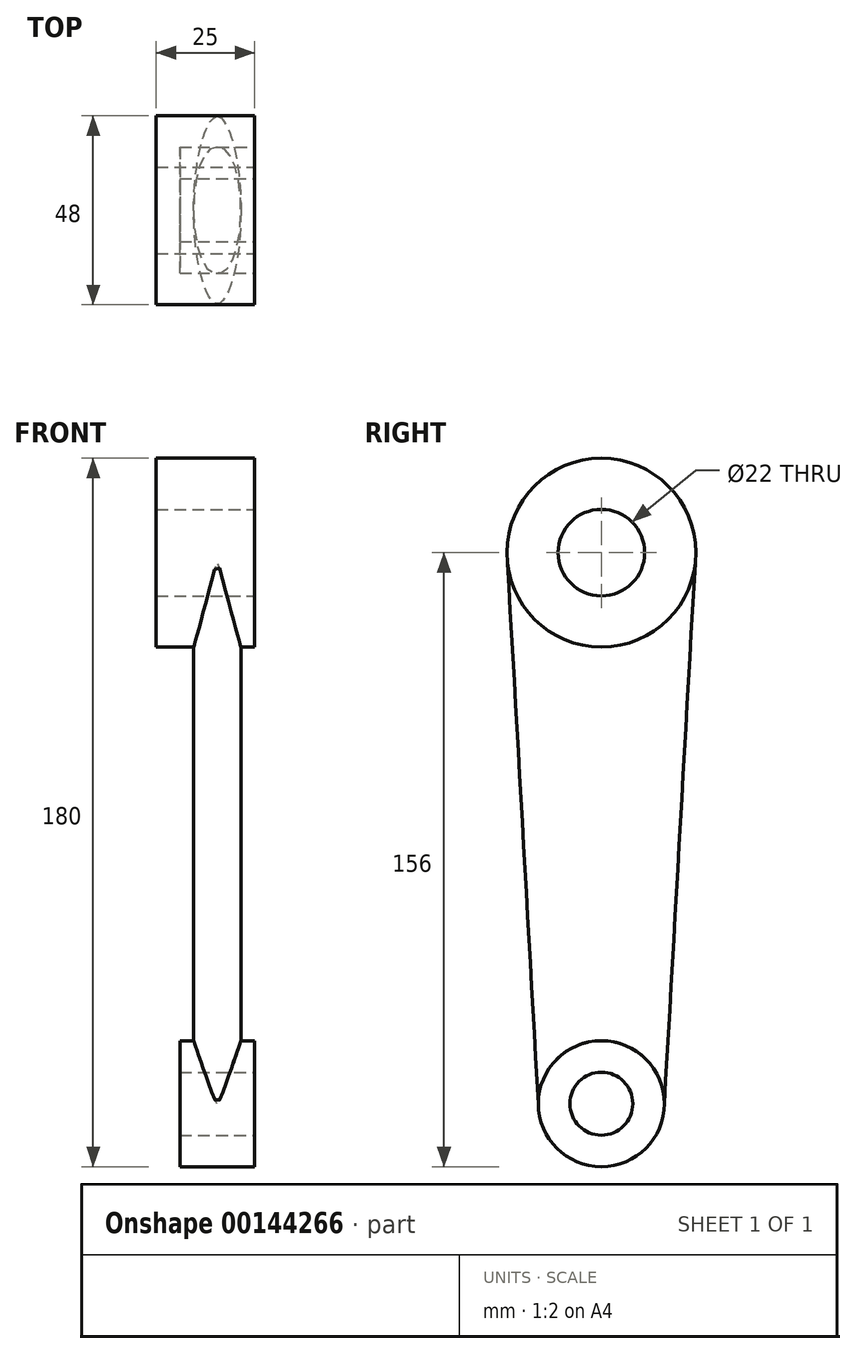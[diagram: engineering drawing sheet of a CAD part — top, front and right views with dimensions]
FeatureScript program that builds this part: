
annotation { "Feature Type Name" : "Feature", "Feature Type Description" : "" }
export const myFeature = defineFeature(function(context is Context, id is Id, definition is map)
    precondition{}
    {
        {
            var Q0;
            Q0=qCreatedBy(makeId("Right.planeOp"),FACE);
            var sketch = newSketch(context, id + "F0", { "sketchPlane" : qUnion([Q0])});
            skCircle(sketch, "E0", {"center": v(0, 0) * mm, "radius": 16 * mm});
            skCircle(sketch, "E1", {"center": v(0, 140) * mm, "radius": 24 * mm});
            skSolve(sketch);
        }
        {
            var Q0;
            Q0=makeQuery(id+"F0.imprint","IMPRINT",FACE,{"disambiguationData":[TD([[makeQuery(id+"F0.imprint","IMPRINT",EDGE,{"derivedFrom":sQuery(id+"F0.wireOp",EDGE,"E1")}),1.0]])]});
            extrude(context, id + "F1", {"entities" : qUnion([Q0]), "oppositeDirection" : true, "depth" : 25 * mm});
        }
        {
            var Q0;
            Q0=makeQuery(id+"F0.imprint","IMPRINT",FACE,{"disambiguationData":[TD([[makeQuery(id+"F0.imprint","IMPRINT",EDGE,{"derivedFrom":sQuery(id+"F0.wireOp",EDGE,"E0")}),1.0]])]});
            extrude(context, id + "F2", {"entities" : qUnion([Q0]), "oppositeDirection" : true, "depth" : 19 * mm});
        }
        {
            var Q0;
            Q0=qCreatedBy(makeId("Top.planeOp"),FACE);
            var sketch = newSketch(context, id + "F3", { "sketchPlane" : qUnion([Q0])});
            skEllipse(sketch, "E2", {"center": v(-9.5, 0) * mm, "majorRadius": 16 * mm, "minorRadius": 6 * mm, "majorAxis": v(0, 1)});
            skPoint(sketch, "E3", {"position": v(-15.5, 0) * mm});
            skLineSegment(sketch, "E4", {"start": v(-19, 16) * mm, "end": v(0, 16) * mm, "construction": true});
            skSolve(sketch);
        }
        {
            var Q0;
            Q0=sQuery(id+"F0.wireOp",VERTEX,"E1.center");
            var Q1;
            Q1=qCreatedBy(makeId("Top.planeOp"),FACE);
            cPlane(context, id + "F4", {"entities" : qUnion([Q0, Q1]), "cplaneType" : CPlaneType.PLANE_POINT, "offset" : 25 * mm, "width" : 150 * mm, "height" : 150 * mm});
        }
        {
            var Q0;
            Q0=qCreatedBy(id+"F4.planeOp",FACE);
            var sketch = newSketch(context, id + "F5", { "sketchPlane" : qUnion([Q0])});
            skEllipse(sketch, "E5", {"center": v(-9.5, 0) * mm, "majorRadius": 24 * mm, "minorRadius": 6 * mm, "majorAxis": v(0, 1)});
            skLineSegment(sketch, "E6", {"start": v(-25, 24) * mm, "end": v(0, 24) * mm, "construction": true});
            skSolve(sketch);
        }
        {
            var Q2;
            Q2=makeQuery(id+"F5.imprint","IMPRINT",FACE,{"disambiguationData":[TD([[makeQuery(id+"F5.imprint","IMPRINT",EDGE,{"derivedFrom":sQuery(id+"F5.wireOp",EDGE,"E5")}),1.0]])]});
            var Q3;
            Q3=makeQuery(id+"F3.imprint","IMPRINT",FACE,{"disambiguationData":[TD([[makeQuery(id+"F3.imprint","IMPRINT",EDGE,{"derivedFrom":sQuery(id+"F3.wireOp",EDGE,"E2")}),1.0]])]});
            loft(context, id + "F6", {"operationType" : NewBodyOperationType.ADD, "sheetProfilesArray" : [{ "sheetProfileEntities" : qUnion([Q2]) }, { "sheetProfileEntities" : qUnion([Q3]) }]});
        }
        {
            var Q0;
            Q0=makeQuery(id+"F0.imprint","IMPRINT",FACE,{"disambiguationData":[TD([[makeQuery(id+"F0.imprint","IMPRINT",EDGE,{"derivedFrom":sQuery(id+"F0.wireOp",EDGE,"E1")}),1.0]])]});
            var sketch = newSketch(context, id + "F7", { "sketchPlane" : qUnion([Q0])});
            skCircle(sketch, "E7", {"center": v(0, 140) * mm, "radius": 11 * mm});
            skCircle(sketch, "E8", {"center": v(0, 0) * mm, "radius": 8 * mm});
            skSolve(sketch);
        }
        {
            var Q0;
            Q0 = qSketchRegion(id + "F7", true);
            extrude(context, id + "F8", {"entities" : qUnion([Q0]), "operationType" : NewBodyOperationType.REMOVE, "endBound" : BoundingType.THROUGH_ALL, "oppositeDirection" : true, "depth" : 25 * mm});
        }
    });
